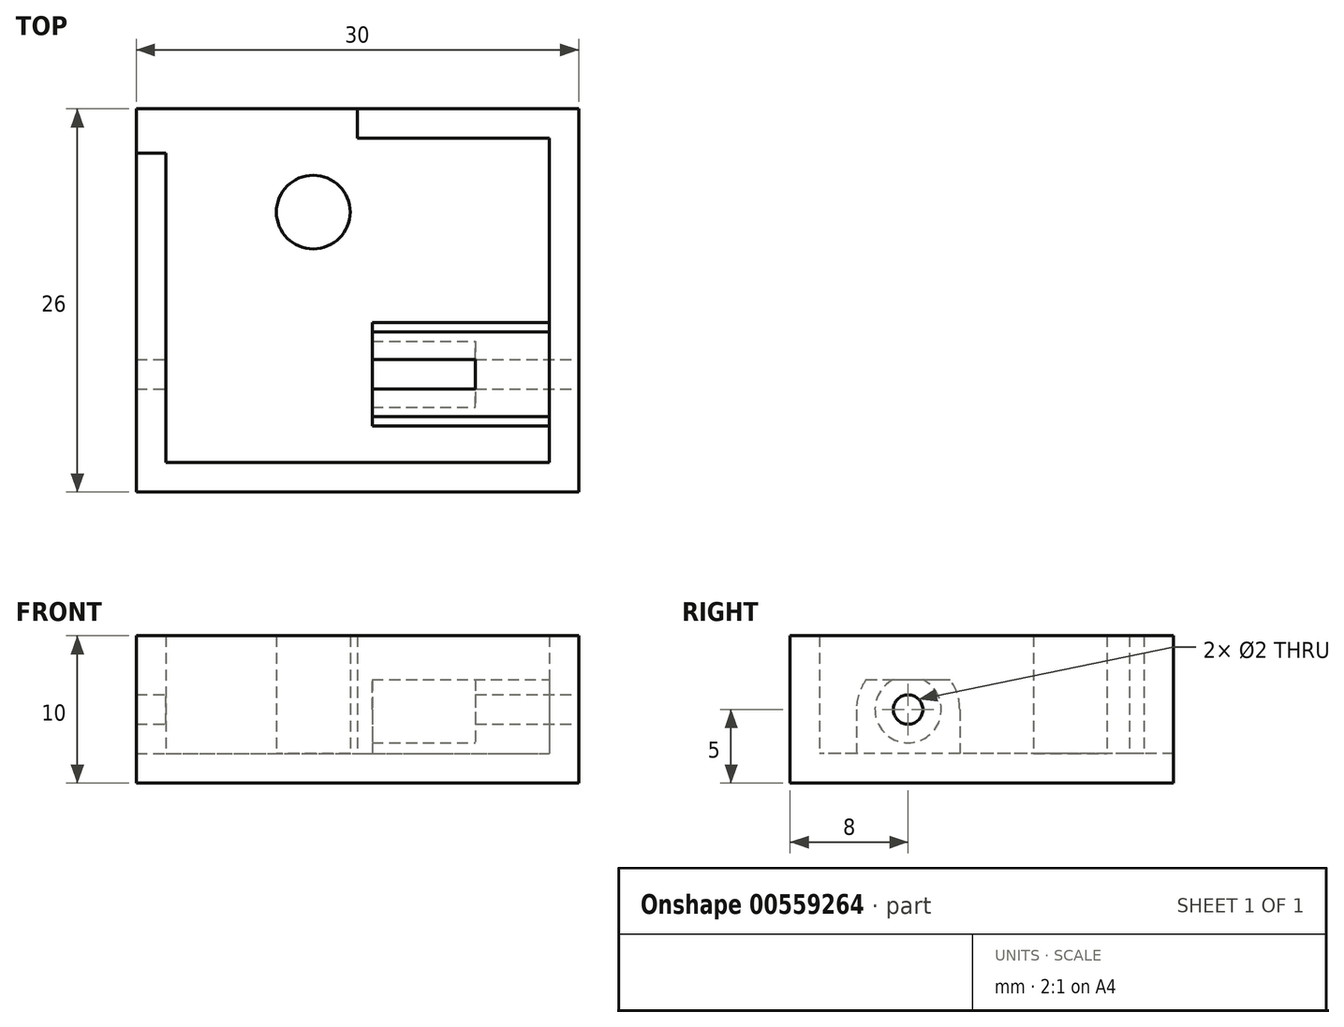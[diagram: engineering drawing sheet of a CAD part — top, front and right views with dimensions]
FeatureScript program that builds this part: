
annotation { "Feature Type Name" : "Feature", "Feature Type Description" : "" }
export const myFeature = defineFeature(function(context is Context, id is Id, definition is map)
    precondition{}
    {
        {
            var Q0;
            Q0=qCreatedBy(makeId("Top.planeOp"),FACE);
            var sketch = newSketch(context, id + "F0", { "sketchPlane" : qUnion([Q0])});
            skLineSegment(sketch, "E0.bottom", {"start": v(-15, 13) * mm, "end": v(15, 13) * mm});
            skLineSegment(sketch, "E0.top", {"start": v(-15, -13) * mm, "end": v(15, -13) * mm});
            skLineSegment(sketch, "E0.left", {"start": v(-15, 13) * mm, "end": v(-15, -13) * mm});
            skLineSegment(sketch, "E0.right", {"start": v(15, 13) * mm, "end": v(15, -13) * mm});
            skPoint(sketch, "E0.middle", {"position": v(0, 0) * mm});
            skSolve(sketch);
        }
        {
            var Q0;
            Q0=qSketchRegion(id+"F0",true);
            extrude(context, id + "F1", {"entities" : qUnion([Q0]), "depth" : 2 * mm, "offsetDistance" : 25 * mm});
        }
        {
            var Q0;
            Q0=makeQuery(id+"F1.opExtrude","CAP_FACE",FACE,{"disambiguationData":[OSD([sQuery(id+"F0.wireOp",EDGE,"E0.bottom"),sQuery(id+"F0.wireOp",EDGE,"E0.top"),sQuery(id+"F0.wireOp",EDGE,"E0.left"),sQuery(id+"F0.wireOp",EDGE,"E0.right")])],"isStart":false});
            var sketch = newSketch(context, id + "F2", { "sketchPlane" : qUnion([Q0])});
            skLineSegment(sketch, "E1.top", {"start": v(-15, -13) * mm, "end": v(15, -13) * mm});
            skLineSegment(sketch, "E1.right", {"start": v(15, 13) * mm, "end": v(15, -13) * mm});
            skLineSegment(sketch, "E2.2", {"start": v(-13, -11) * mm, "end": v(13, -11) * mm});
            skLineSegment(sketch, "E2.3", {"start": v(13, 11) * mm, "end": v(13, -11) * mm});
            skLineSegment(sketch, "E3.trimOffspring", {"start": v(-13, 10) * mm, "end": v(-13, -11) * mm});
            skLineSegment(sketch, "E4", {"start": v(-15, 10) * mm, "end": v(-15, -13) * mm});
            skLineSegment(sketch, "E5", {"start": v(0, 13) * mm, "end": v(0, 11) * mm});
            skLineSegment(sketch, "E6.trimOffspring", {"start": v(0, 13) * mm, "end": v(15, 13) * mm});
            skLineSegment(sketch, "E7.trimOffspring", {"start": v(0, 11) * mm, "end": v(13, 11) * mm});
            skLineSegment(sketch, "E8", {"start": v(-15, 10) * mm, "end": v(-13, 10) * mm});
            skSolve(sketch);
        }
        {
            var Q0;
            Q0=qSketchRegion(id+"F2",true);
            extrude(context, id + "F3", {"entities" : qUnion([Q0]), "operationType" : NewBodyOperationType.ADD, "depth" : 8 * mm, "offsetDistance" : 25 * mm});
        }
        {
            var Q0;
            Q0=makeQuery(id+"F1.opExtrude","CAP_FACE",FACE,{"disambiguationData":[OSD([sQuery(id+"F0.wireOp",EDGE,"E0.bottom"),sQuery(id+"F0.wireOp",EDGE,"E0.top"),sQuery(id+"F0.wireOp",EDGE,"E0.left"),sQuery(id+"F0.wireOp",EDGE,"E0.right")])],"isStart":false});
            var sketch = newSketch(context, id + "F4", { "sketchPlane" : qUnion([Q0])});
            skCircle(sketch, "E9", {"center": v(-3, 6) * mm, "radius": 2.5 * mm});
            skLineSegment(sketch, "E10", {"start": v(-3, 11) * mm, "end": v(-3, 0) * mm, "construction": true});
            skSolve(sketch);
        }
        {
            var Q0;
            Q0=qSketchRegion(id+"F4",true);
            var Q1;
            Q1=makeQuery(id+"F3.opExtrude","CAP_FACE",FACE,{"disambiguationData":[OSD([sQuery(id+"F2.wireOp",EDGE,"E1.bottom"),sQuery(id+"F2.wireOp",EDGE,"E1.top"),sQuery(id+"F2.wireOp",EDGE,"E1.right"),sQuery(id+"F2.wireOp",EDGE,"E2.0"),sQuery(id+"F2.wireOp",EDGE,"E2.2"),sQuery(id+"F2.wireOp",EDGE,"E2.3"),sQuery(id+"F2.wireOp",EDGE,"E3.trimOffspring"),sQuery(id+"F2.wireOp",EDGE,"E4"),sQuery(id+"F2.wireOp",EDGE,"QNV54tgF-Zadq-EhpF-mVKo-s3rOeFkCFm37"),sQuery(id+"F2.wireOp",EDGE,"E5"),sQuery(id+"F2.wireOp",EDGE,"E6.trimOffspring"),sQuery(id+"F2.wireOp",EDGE,"E7.trimOffspring")])],"isStart":false});
            extrude(context, id + "F5", {"entities" : qUnion([Q0]), "operationType" : NewBodyOperationType.ADD, "endBound" : BoundingType.UP_TO_SURFACE, "depth" : 12 * mm, "endBoundEntityFace" : qUnion([Q1]), "offsetDistance" : 25 * mm});
        }
        {
            var Q0;
            Q0=makeQuery(id+"F3.opExtrude","SWEPT_FACE",FACE,{"disambiguationData":[OSD([sQuery(id+"F2.wireOp",EDGE,"E2.3")])]});
            var sketch = newSketch(context, id + "F6", { "sketchPlane" : qUnion([Q0])});
            skLineSegment(sketch, "E11.top", {"start": v(1.5, 5) * mm, "end": v(8.5, 5) * mm, "construction": true});
            skPoint(sketch, "E12.centerSnap0", {"position": v(5, 5) * mm});
            skArc(sketch, "E13", {"start": v(8.5, 5) * mm, "mid": v(8.34, 6.06) * mm, "end": v(7.86, 7.02) * mm});
            skLineSegment(sketch, "E14", {"start": v(8.5, 5) * mm, "end": v(8.5, 0) * mm});
            skLineSegment(sketch, "E15", {"start": v(1.5, 5) * mm, "end": v(1.5, 0) * mm});
            skLineSegment(sketch, "E16", {"start": v(8.5, 0) * mm, "end": v(1.5, 0) * mm});
            skArc(sketch, "E17", {"start": v(4, 7.02) * mm, "mid": v(5, 2.75) * mm, "end": v(6, 7.02) * mm});
            skLineSegment(sketch, "E18", {"start": v(7.86, 7.02) * mm, "end": v(6, 7.02) * mm});
            skLineSegment(sketch, "E19.trimOffspring", {"start": v(4, 7.02) * mm, "end": v(2.14, 7.02) * mm});
            skArc(sketch, "E20.trimOffspring", {"start": v(2.14, 7.02) * mm, "mid": v(1.66, 6.06) * mm, "end": v(1.5, 5) * mm});
            skSolve(sketch);
        }
        {
            var Q0;
            Q0=qSketchRegion(id+"F6",true);
            extrude(context, id + "F7", {"entities" : qUnion([Q0]), "operationType" : NewBodyOperationType.ADD, "depth" : 12 * mm, "offsetDistance" : 25 * mm});
        }
        {
            var Q0;
            {var subQ1=sQuery(id+"F2.wireOp",EDGE,"E2.3");var subQ2=sQuery(id+"F2.wireOp",EDGE,"E2.2");Q0=makeQuery(id+"F7.boolean.opBoolean","SPLIT",FACE,{"disambiguationData":[TD([makeQuery(id+"F3.opExtrude","SWEPT_FACE",FACE,{"disambiguationData":[OSD([subQ2])]})])],"derivedFrom":makeQuery(id+"F3.opExtrude","SWEPT_FACE",FACE,{"disambiguationData":[OSD([subQ1])]})});}
            var sketch = newSketch(context, id + "F8", { "sketchPlane" : qUnion([Q0])});
            skLineSegment(sketch, "E21", {"start": v(8.5, 2) * mm, "end": v(8.5, 5) * mm});
            skLineSegment(sketch, "E22", {"start": v(1.5, 2) * mm, "end": v(8.5, 2) * mm});
            skLineSegment(sketch, "E23", {"start": v(8.5, 5) * mm, "end": v(8.5, 5) * mm});
            skLineSegment(sketch, "E24", {"start": v(1.5, 2) * mm, "end": v(1.5, 5) * mm});
            skLineSegment(sketch, "E25", {"start": v(7.86, 7.02) * mm, "end": v(2.14, 7.02) * mm});
            skArc(sketch, "E26", {"start": v(8.5, 5) * mm, "mid": v(8.34, 6.06) * mm, "end": v(7.86, 7.02) * mm});
            skArc(sketch, "E27", {"start": v(2.14, 7.02) * mm, "mid": v(1.66, 6.06) * mm, "end": v(1.5, 5) * mm});
            skSolve(sketch);
        }
        {
            var Q0;
            Q0 = qSketchRegion(id + "F8", true);
            extrude(context, id + "F9", {"entities" : qUnion([Q0]), "operationType" : NewBodyOperationType.ADD, "depth" : 5 * mm, "offsetDistance" : 25 * mm});
        }
        {
            var Q0;
            Q0=makeQuery(id+"F3.boolean.opBoolean","MERGE",FACE,{"derivedFrom":[makeQuery(id+"F1.opExtrude","SWEPT_FACE",FACE,{"disambiguationData":[OSD([sQuery(id+"F0.wireOp",EDGE,"E0.right")])]}),makeQuery(id+"F3.opExtrude","SWEPT_FACE",FACE,{"disambiguationData":[OSD([sQuery(id+"F2.wireOp",EDGE,"E1.right")])]})]});
            var sketch = newSketch(context, id + "F10", { "sketchPlane" : qUnion([Q0])});
            skCircle(sketch, "E28", {"center": v(-5, 5) * mm, "radius": 1 * mm});
            skSolve(sketch);
        }
        {
            var Q0;
            Q0 = qSketchRegion(id + "F10", true);
            extrude(context, id + "F11", {"entities" : qUnion([Q0]), "operationType" : NewBodyOperationType.REMOVE, "endBound" : BoundingType.THROUGH_ALL, "oppositeDirection" : true, "depth" : 25 * mm, "offsetDistance" : 25 * mm});
        }
    });
